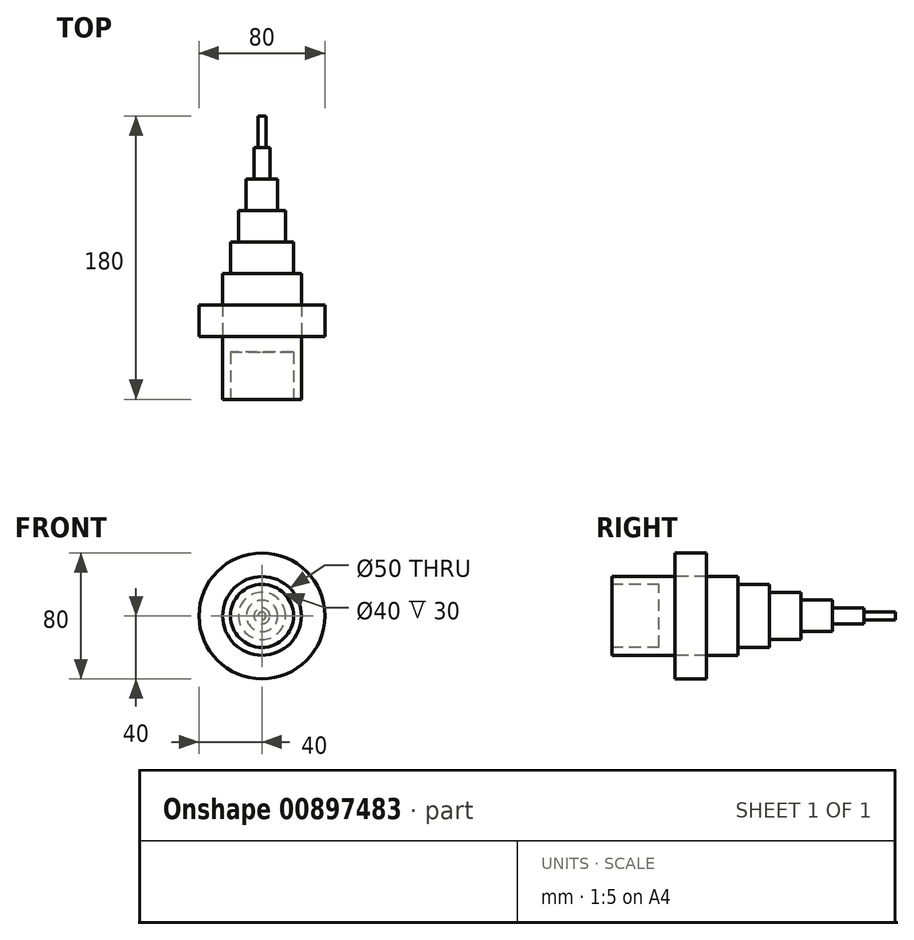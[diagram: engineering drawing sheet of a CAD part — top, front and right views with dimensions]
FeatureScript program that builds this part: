
annotation { "Feature Type Name" : "Feature", "Feature Type Description" : "" }
export const myFeature = defineFeature(function(context is Context, id is Id, definition is map)
    precondition{}
    {
        {
            var Q0;
            Q0=qCreatedBy(makeId("Front.planeOp"),FACE);
            var sketch = newSketch(context, id + "F0", { "sketchPlane" : qUnion([Q0])});
            skCircle(sketch, "E0", {"center": v(0, 0) * mm, "radius": 25 * mm});
            skSolve(sketch);
        }
        {
            var Q0;
            Q0=makeQuery(id+"F0.imprint","IMPRINT",FACE,{"disambiguationData":[TD([[makeQuery(id+"F0.imprint","IMPRINT",EDGE,{"derivedFrom":sQuery(id+"F0.wireOp",EDGE,"E0")}),1.0]])]});
            extrude(context, id + "F1", {"entities" : qUnion([Q0]), "depth" : 40 * mm, "offsetDistance" : 25.4 * mm});
        }
        {
            var Q0;
            Q0=makeQuery(id+"F1.opExtrude","CAP_FACE",FACE,{"disambiguationData":[OSD([sQuery(id+"F0.wireOp",EDGE,"E0")])],"isStart":false});
            var sketch = newSketch(context, id + "F2", { "sketchPlane" : qUnion([Q0])});
            skCircle(sketch, "E1", {"center": v(0, 0) * mm, "radius": 20 * mm});
            skSolve(sketch);
        }
        {
            var Q0;
            Q0=makeQuery(id+"F2.imprint","IMPRINT",FACE,{"disambiguationData":[TD([[makeQuery(id+"F2.imprint","IMPRINT",EDGE,{"derivedFrom":sQuery(id+"F2.wireOp",EDGE,"E1")}),1.0]])]});
            extrude(context, id + "F3", {"entities" : qUnion([Q0]), "operationType" : NewBodyOperationType.REMOVE, "oppositeDirection" : true, "depth" : 30 * mm, "offsetDistance" : 25.4 * mm});
        }
        {
            var Q0;
            Q0=makeQuery(id+"F1.opExtrude","CAP_FACE",FACE,{"disambiguationData":[OSD([sQuery(id+"F0.wireOp",EDGE,"E0")])],"isStart":true});
            var sketch = newSketch(context, id + "F4", { "sketchPlane" : qUnion([Q0])});
            skCircle(sketch, "E2", {"center": v(0, 0) * mm, "radius": 40 * mm});
            skSolve(sketch);
        }
        {
            var Q0;
            Q0=makeQuery(id+"F4.imprint","IMPRINT",FACE,{"disambiguationData":[TD([[makeQuery(id+"F4.imprint","IMPRINT",EDGE,{"derivedFrom":sQuery(id+"F4.wireOp",EDGE,"E2")}),1.0]])]});
            extrude(context, id + "F5", {"entities" : qUnion([Q0]), "depth" : 20 * mm, "offsetDistance" : 25.4 * mm});
        }
        {
            var Q0;
            Q0=makeQuery(id+"F5.opExtrude","CAP_FACE",FACE,{"disambiguationData":[OSD([sQuery(id+"F0.wireOp",EDGE,"E0"),sQuery(id+"F4.wireOp",EDGE,"E2")])],"isStart":false});
            var sketch = newSketch(context, id + "F6", { "sketchPlane" : qUnion([Q0])});
            skCircle(sketch, "E3", {"center": v(0, 0) * mm, "radius": 25 * mm});
            skSolve(sketch);
        }
        {
            var Q0;
            Q0=makeQuery(id+"F6.imprint","IMPRINT",FACE,{"disambiguationData":[TD([[makeQuery(id+"F6.imprint","IMPRINT",EDGE,{"derivedFrom":sQuery(id+"F6.wireOp",EDGE,"E3")}),-1.0]])]});
            extrude(context, id + "F7", {"entities" : qUnion([Q0]), "depth" : 20 * mm, "offsetDistance" : 25.4 * mm});
        }
        {
            var Q0;
            Q0=makeQuery(id+"F7.opExtrude","CAP_FACE",FACE,{"disambiguationData":[OSD([sQuery(id+"F6.wireOp",EDGE,"E3")])],"isStart":false});
            var sketch = newSketch(context, id + "F8", { "sketchPlane" : qUnion([Q0])});
            skCircle(sketch, "E4", {"center": v(0, 0) * mm, "radius": 20 * mm});
            skSolve(sketch);
        }
        {
            var Q0;
            Q0=makeQuery(id+"F8.imprint","IMPRINT",FACE,{"disambiguationData":[TD([[makeQuery(id+"F8.imprint","IMPRINT",EDGE,{"derivedFrom":sQuery(id+"F8.wireOp",EDGE,"E4")}),1.0]])]});
            extrude(context, id + "F9", {"entities" : qUnion([Q0]), "operationType" : NewBodyOperationType.ADD, "depth" : 20 * mm, "offsetDistance" : 25.4 * mm});
        }
        {
            var Q0;
            Q0=makeQuery(id+"F9.opExtrude","CAP_FACE",FACE,{"disambiguationData":[OSD([sQuery(id+"F8.wireOp",EDGE,"E4")])],"isStart":false});
            var sketch = newSketch(context, id + "F10", { "sketchPlane" : qUnion([Q0])});
            skCircle(sketch, "E5", {"center": v(0, 0) * mm, "radius": 15 * mm});
            skSolve(sketch);
        }
        {
            var Q0;
            Q0=makeQuery(id+"F10.imprint","IMPRINT",FACE,{"disambiguationData":[TD([[makeQuery(id+"F10.imprint","IMPRINT",EDGE,{"derivedFrom":sQuery(id+"F10.wireOp",EDGE,"E5")}),1.0]])]});
            extrude(context, id + "F11", {"entities" : qUnion([Q0]), "operationType" : NewBodyOperationType.ADD, "depth" : 20 * mm, "offsetDistance" : 25.4 * mm});
        }
        {
            var Q0;
            Q0=makeQuery(id+"F11.opExtrude","CAP_FACE",FACE,{"disambiguationData":[OSD([sQuery(id+"F10.wireOp",EDGE,"E5")])],"isStart":false});
            var sketch = newSketch(context, id + "F12", { "sketchPlane" : qUnion([Q0])});
            skCircle(sketch, "E6", {"center": v(0, 0) * mm, "radius": 10 * mm});
            skSolve(sketch);
        }
        {
            var Q0;
            Q0 = qSketchRegion(id + "F12", true);
            extrude(context, id + "F13", {"entities" : qUnion([Q0]), "operationType" : NewBodyOperationType.ADD, "depth" : 20 * mm, "offsetDistance" : 25.4 * mm});
        }
        {
            var Q0;
            Q0=makeQuery(id+"F13.opExtrude","CAP_FACE",FACE,{"disambiguationData":[OSD([sQuery(id+"F12.wireOp",EDGE,"E6")])],"isStart":false});
            var sketch = newSketch(context, id + "F14", { "sketchPlane" : qUnion([Q0])});
            skCircle(sketch, "E7", {"center": v(0, 0) * mm, "radius": 5 * mm});
            skSolve(sketch);
        }
        {
            var Q0;
            Q0=makeQuery(id+"F14.imprint","IMPRINT",FACE,{"disambiguationData":[TD([[makeQuery(id+"F14.imprint","IMPRINT",EDGE,{"derivedFrom":sQuery(id+"F14.wireOp",EDGE,"E7")}),1.0]])]});
            extrude(context, id + "F15", {"entities" : qUnion([Q0]), "operationType" : NewBodyOperationType.ADD, "depth" : 20 * mm, "offsetDistance" : 25.4 * mm});
        }
        {
            var Q0;
            Q0=makeQuery(id+"F15.opExtrude","CAP_FACE",FACE,{"disambiguationData":[OSD([sQuery(id+"F14.wireOp",EDGE,"E7")])],"isStart":false});
            var sketch = newSketch(context, id + "F16", { "sketchPlane" : qUnion([Q0])});
            skCircle(sketch, "E8", {"center": v(0, 0) * mm, "radius": 2.5 * mm});
            skSolve(sketch);
        }
        {
            var Q0;
            Q0=makeQuery(id+"F16.imprint","IMPRINT",FACE,{"disambiguationData":[TD([[makeQuery(id+"F16.imprint","IMPRINT",EDGE,{"derivedFrom":sQuery(id+"F16.wireOp",EDGE,"E8")}),1.0]])]});
            extrude(context, id + "F17", {"entities" : qUnion([Q0]), "operationType" : NewBodyOperationType.ADD, "depth" : 20 * mm, "offsetDistance" : 25.4 * mm});
        }
    });
